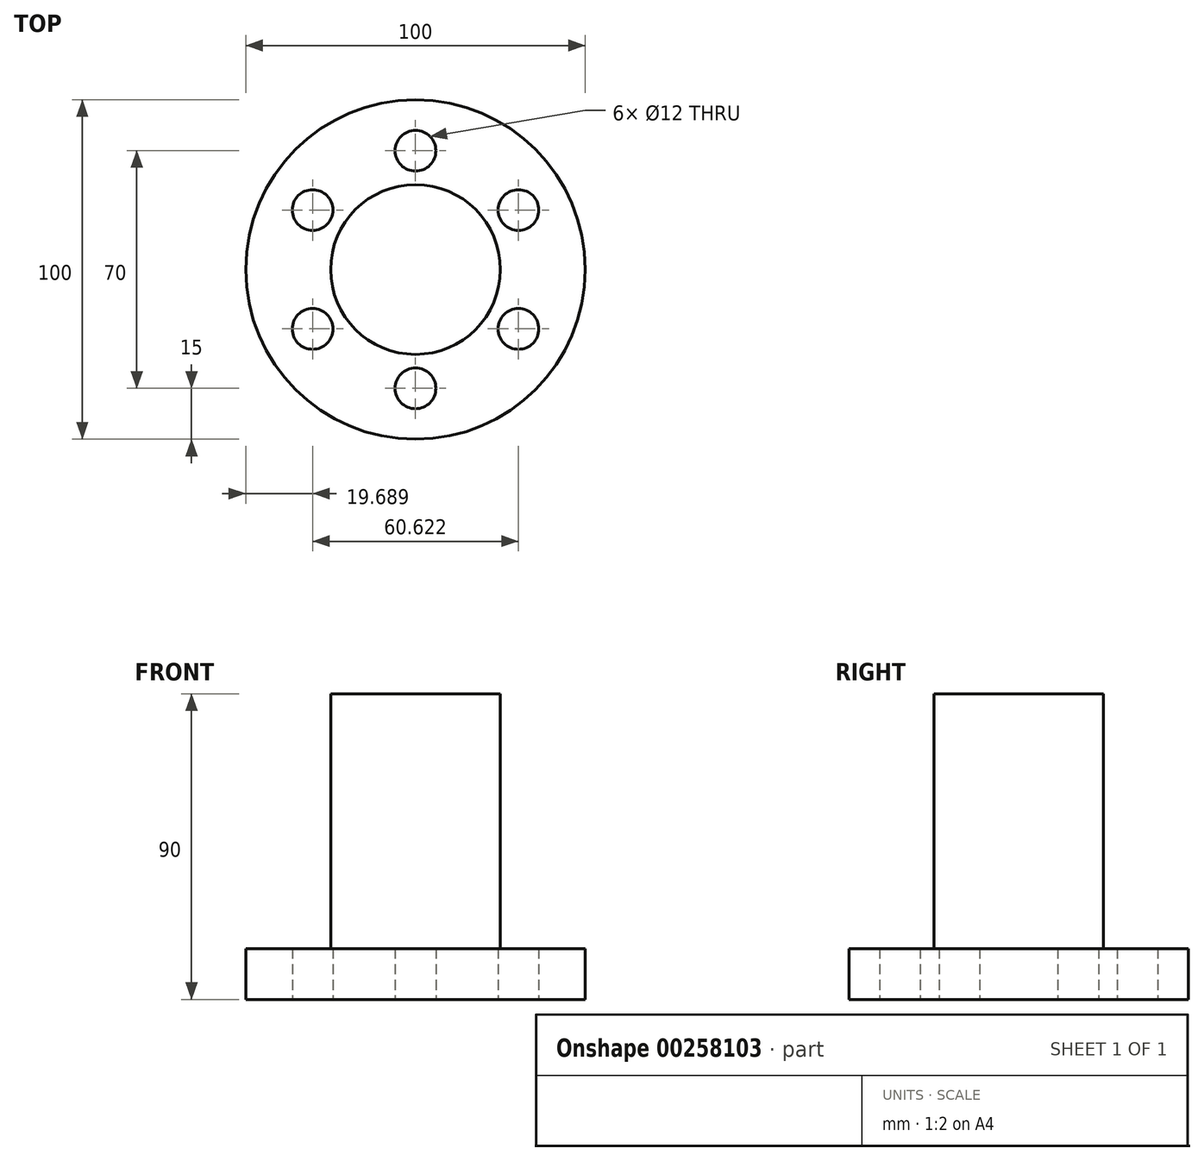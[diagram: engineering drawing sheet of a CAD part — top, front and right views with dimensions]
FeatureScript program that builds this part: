
annotation { "Feature Type Name" : "Feature", "Feature Type Description" : "" }
export const myFeature = defineFeature(function(context is Context, id is Id, definition is map)
    precondition{}
    {
        {
            var Q0;
            Q0=qCreatedBy(makeId("Top.planeOp"),FACE);
            var sketch = newSketch(context, id + "F0", { "sketchPlane" : qUnion([Q0])});
            skCircle(sketch, "E0", {"center": v(0, 0) * mm, "radius": 50 * mm});
            skLineSegment(sketch, "E1", {"start": v(0, 0) * mm, "end": v(0, 57.4) * mm, "construction": true});
            skCircle(sketch, "E2", {"center": v(0, 35) * mm, "radius": 6 * mm});
            skCircle(sketch, "E3", {"center": v(0, 0) * mm, "radius": 35 * mm, "construction": true});
            skCircle(sketch, "E4.1.0", {"center": v(-30.31, 17.5) * mm, "radius": 6 * mm});
            skCircle(sketch, "E4.2.0", {"center": v(-30.31, -17.5) * mm, "radius": 6 * mm});
            skCircle(sketch, "E4.3.0", {"center": v(0, -35) * mm, "radius": 6 * mm});
            skCircle(sketch, "E4.4.0", {"center": v(30.31, -17.5) * mm, "radius": 6 * mm});
            skCircle(sketch, "E4.5.0", {"center": v(30.31, 17.5) * mm, "radius": 6 * mm});
            skSolve(sketch);
        }
        {
            var Q0;
            Q0=makeQuery(id+"F0.imprint","IMPRINT",FACE,{"disambiguationData":[TD([[makeQuery(id+"F0.imprint","IMPRINT",EDGE,{"derivedFrom":sQuery(id+"F0.wireOp",EDGE,"E0")}),1.0]])]});
            extrude(context, id + "F1", {"entities" : qUnion([Q0]), "depth" : 15 * mm});
        }
        {
            var Q0;
            Q0=makeQuery(id+"F1.opExtrude","CAP_FACE",FACE,{"disambiguationData":[OSD([sQuery(id+"F0.wireOp",EDGE,"E0"),sQuery(id+"F0.wireOp",EDGE,"E2"),sQuery(id+"F0.wireOp",EDGE,"E4.1.0"),sQuery(id+"F0.wireOp",EDGE,"E4.2.0"),sQuery(id+"F0.wireOp",EDGE,"E4.3.0"),sQuery(id+"F0.wireOp",EDGE,"E4.4.0"),sQuery(id+"F0.wireOp",EDGE,"E4.5.0")])],"isStart":false});
            var sketch = newSketch(context, id + "F2", { "sketchPlane" : qUnion([Q0])});
            skCircle(sketch, "E5", {"center": v(0, 0) * mm, "radius": 25 * mm});
            skSolve(sketch);
        }
        {
            var Q0;
            Q0=makeQuery(id+"F2.imprint","IMPRINT",FACE,{"disambiguationData":[TD([[makeQuery(id+"F2.imprint","IMPRINT",EDGE,{"derivedFrom":sQuery(id+"F2.wireOp",EDGE,"E5")}),1.0]])]});
            extrude(context, id + "F3", {"entities" : qUnion([Q0]), "operationType" : NewBodyOperationType.ADD, "depth" : 75 * mm});
        }
    });
